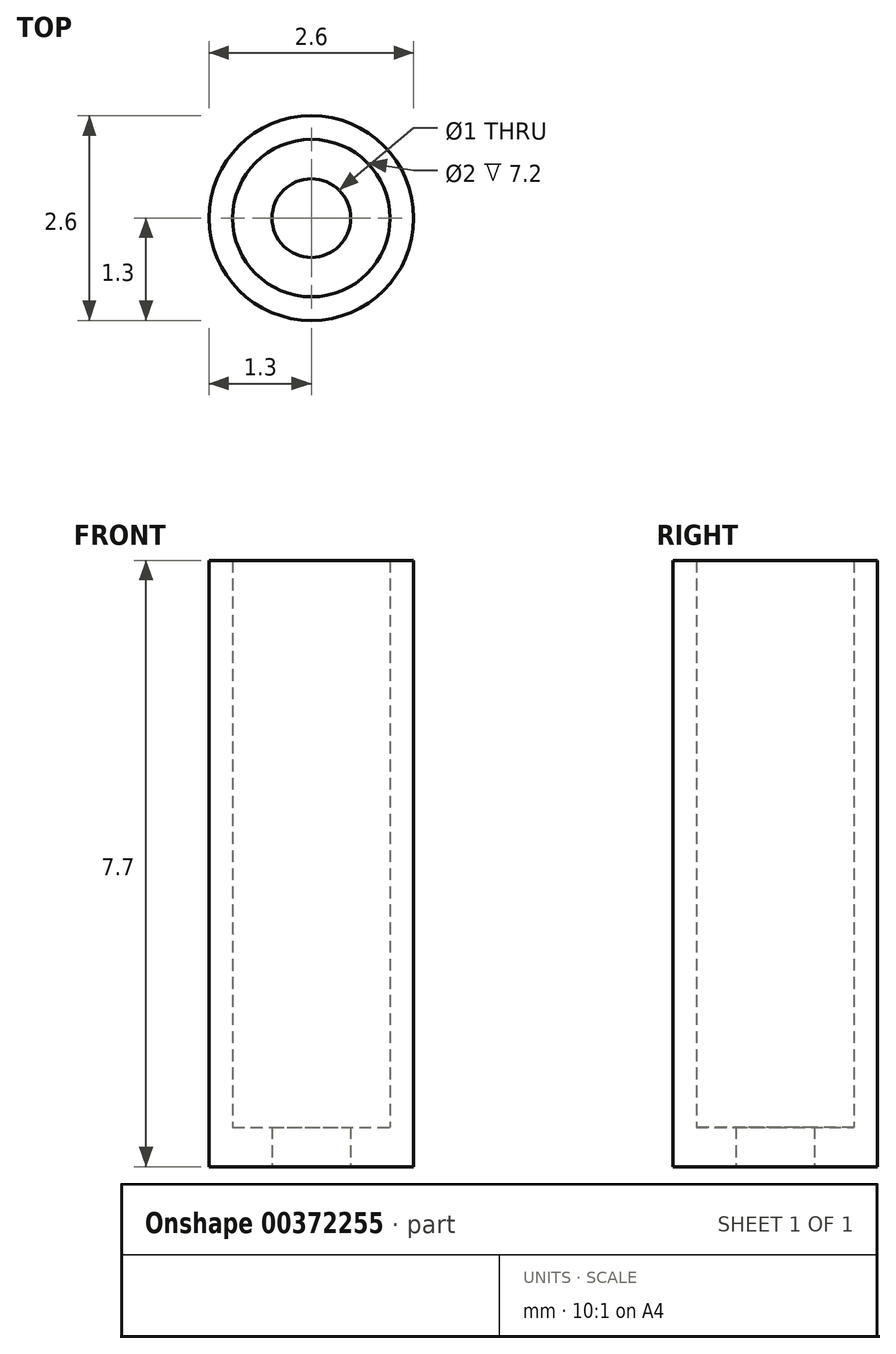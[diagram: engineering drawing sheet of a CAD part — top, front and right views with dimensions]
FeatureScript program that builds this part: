
annotation { "Feature Type Name" : "Feature", "Feature Type Description" : "" }
export const myFeature = defineFeature(function(context is Context, id is Id, definition is map)
    precondition{}
    {
        {
            var Q0;
            Q0=qCreatedBy(makeId("Front.planeOp"),FACE);
            var sketch = newSketch(context, id + "F0", { "sketchPlane" : qUnion([Q0])});
            skLineSegment(sketch, "E0", {"start": v(0.5, 0) * mm, "end": v(0.5, 0.5) * mm});
            skLineSegment(sketch, "E1", {"start": v(0.5, 0.5) * mm, "end": v(1, 0.5) * mm});
            skLineSegment(sketch, "E2", {"start": v(1, 0.5) * mm, "end": v(1, 7.7) * mm});
            skLineSegment(sketch, "E3", {"start": v(1, 7.7) * mm, "end": v(1.3, 7.7) * mm});
            skLineSegment(sketch, "E4", {"start": v(1.3, 7.7) * mm, "end": v(1.3, 0) * mm});
            skLineSegment(sketch, "E5", {"start": v(1.3, 0) * mm, "end": v(0.5, 0) * mm});
            skLineSegment(sketch, "E6", {"start": v(0, 0) * mm, "end": v(0, 7.7) * mm, "construction": true});
            skSolve(sketch);
        }
        {
            var Q0;
            Q0=makeQuery(id+"F0.imprint","IMPRINT",FACE,{"disambiguationData":[TD([[makeQuery(id+"F0.imprint","IMPRINT",EDGE,{"derivedFrom":sQuery(id+"F0.wireOp",EDGE,"E0")}),-1.0]])]});
            var Q1;
            Q1=sQuery(id+"F0.wireOp",EDGE,"E6");
            revolve(context, id + "F1", {"entities" : qUnion([Q0]), "axis" : qUnion([Q1]), "revolveType" : RevolveType.FULL});
        }
    });
